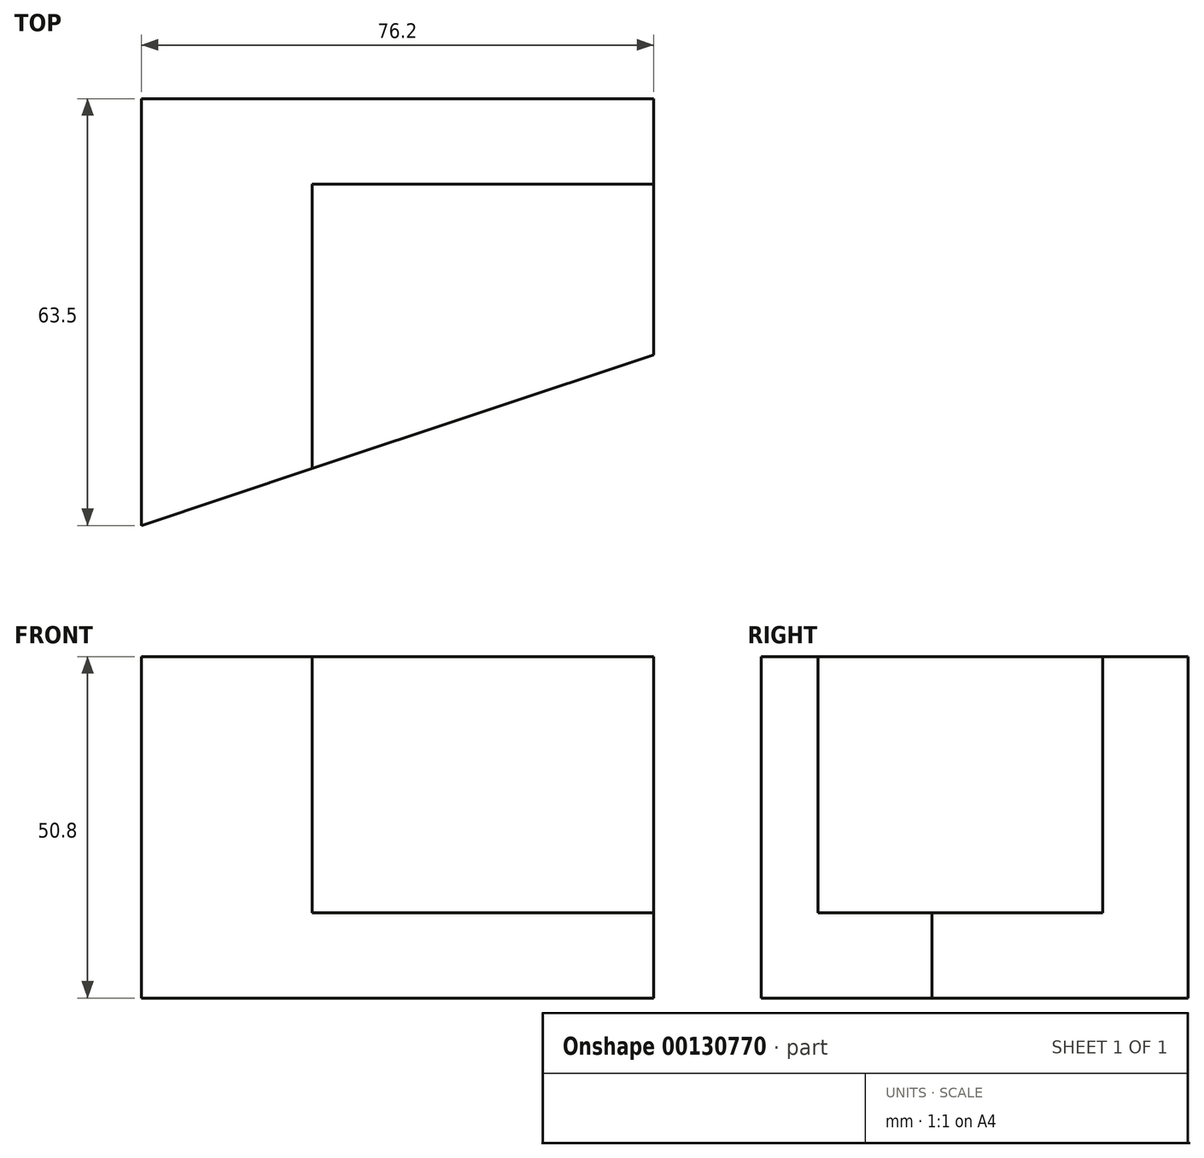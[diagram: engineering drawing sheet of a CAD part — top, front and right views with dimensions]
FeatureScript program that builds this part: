
annotation { "Feature Type Name" : "Feature", "Feature Type Description" : "" }
export const myFeature = defineFeature(function(context is Context, id is Id, definition is map)
    precondition{}
    {
        {
            var Q0;
            Q0=qCreatedBy(makeId("Front.planeOp"),FACE);
            var sketch = newSketch(context, id + "F0", { "sketchPlane" : qUnion([Q0])});
            skLineSegment(sketch, "E0", {"start": v(0, 0) * mm, "end": v(0, 50.8) * mm});
            skLineSegment(sketch, "E1", {"start": v(0, 50.8) * mm, "end": v(76.2, 50.8) * mm});
            skLineSegment(sketch, "E2", {"start": v(76.2, 50.8) * mm, "end": v(76.2, 0) * mm});
            skLineSegment(sketch, "E3", {"start": v(76.2, 0) * mm, "end": v(0, 0) * mm});
            skSolve(sketch);
        }
        {
            var Q0;
            Q0 = qSketchRegion(id + "F0", true);
            extrude(context, id + "F1", {"entities" : qUnion([Q0]), "oppositeDirection" : true, "depth" : 63.5 * mm});
        }
        {
            var Q0;
            Q0=makeQuery(id+"F1.opExtrude","SWEPT_FACE",FACE,{"disambiguationData":[OSD([sQuery(id+"F0.wireOp",EDGE,"E1")])]});
            var sketch = newSketch(context, id + "F2", { "sketchPlane" : qUnion([Q0])});
            skLineSegment(sketch, "E4", {"start": v(0, 0) * mm, "end": v(76.2, 25.4) * mm});
            skSolve(sketch);
        }
        {
            var Q0;
            Q0 = qSketchRegion(id + "F2", true);
            var Q1;
            {var subQ0=sQuery(id+"F2.wireOp",EDGE,"E4");Q1=makeQuery(id+"F2.imprint","IMPRINT",FACE,{"disambiguationData":[TD([[makeQuery(id+"F2.imprint","IMPRINT",EDGE,{"derivedFrom":subQ0}),-1.0]])]});}
            extrude(context, id + "F3", {"entities" : qUnion([Q0, Q1]), "operationType" : NewBodyOperationType.REMOVE, "endBound" : BoundingType.THROUGH_ALL, "oppositeDirection" : true, "depth" : 25.4 * mm});
        }
        {
            var Q0;
            Q0=qCreatedBy(makeId("Front.planeOp"),FACE);
            var sketch = newSketch(context, id + "F4", { "sketchPlane" : qUnion([Q0])});
            skLineSegment(sketch, "E5", {"start": v(25.4, 50.8) * mm, "end": v(25.4, 12.7) * mm});
            skLineSegment(sketch, "E6", {"start": v(25.4, 12.7) * mm, "end": v(76.2, 12.7) * mm});
            skLineSegment(sketch, "E7", {"start": v(76.2, 12.7) * mm, "end": v(76.2, 50.8) * mm});
            skLineSegment(sketch, "E8", {"start": v(76.2, 50.8) * mm, "end": v(25.4, 50.8) * mm});
            skSolve(sketch);
        }
        {
            var Q0;
            Q0 = qSketchRegion(id + "F4", true);
            extrude(context, id + "F5", {"entities" : qUnion([Q0]), "operationType" : NewBodyOperationType.REMOVE, "oppositeDirection" : true, "depth" : 50.8 * mm});
        }
    });
